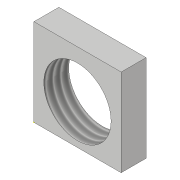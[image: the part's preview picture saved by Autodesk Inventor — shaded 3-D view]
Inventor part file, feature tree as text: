
AUTODESK INVENTOR PART (.ipt)
format: ipt  version: 2019 (Build 230136000, 136)  size: 92,672 bytes
history: native  units: in
note: dims shown in document units (in); Inventor stores cm internally (conversion verified against a paired STEP export)
features: sketch x3, extrude x2, thread x1
ambient origin geometry x8: Origin, YZ Plane, XZ Plane, XY Plane, X Axis, Y Axis, Z Axis, Center Point
bodies: Solid1 (feature_tree)
feature tree (6):
  extrude  "Extrusion1"  Depth=1.378in
  sketch  "Sketch2"  dims[d2=0.3937in d3=0.0in d4=1.063in d5=0.3937in d6=0.0in]
  extrude  "Extrusion2"  Depth=0.3937in
  thread  "Thread1"  [1 undecoded]
  sketch  "Sketch1"  dims[d0=1.378in d1=1.378in]
  sketch  "Sketch3"  dims[d7=0.3937in d8=0.0in]
note: 1 required parameter value undecoded (feature->parameter linkage not recoverable at this tier; creation-order binding heuristic only, values carry confidence <= 0.55)
